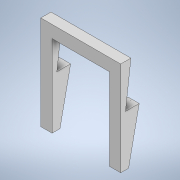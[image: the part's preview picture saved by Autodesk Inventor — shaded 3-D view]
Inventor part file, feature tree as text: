
AUTODESK INVENTOR PART (.ipt)
format: ipt  version: 2022.1 (Build 261234020, 234B)  size: 697,344 bytes
history: native  units: in
note: dims shown in document units (in); Inventor stores cm internally (conversion verified against a paired STEP export)
features: sketch x3, extrude x2, emboss x1
ambient origin geometry x8: Origin, YZ Plane, XZ Plane, XY Plane, X Axis, Y Axis, Z Axis, Center Point
bodies: Body1 (feature_tree)
feature tree (6):
  extrude  "Extrusion6"  Depth=4.0in
  extrude  "Extrusion7"  Depth=0.5in
  emboss  "Emboss1"
  sketch  "Sketch4"  dims[d28=0.5in d29=4.0in]
  sketch  "Sketch6"  dims[d30=4.0in d31=0.5in]
  sketch  "Sketch7"  dims[d32=4.0in d33=5.75in d34=0.624in d35=2.65in d57=4.875in d58=0.0in d59=5.0in d60=3.5in d61=0.0in d62=0.0in d63=0.1in d64=0.0in]
